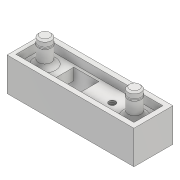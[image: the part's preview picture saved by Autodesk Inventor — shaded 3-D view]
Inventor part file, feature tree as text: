
AUTODESK INVENTOR PART (.ipt)
format: ipt  version: 2018 (Build 220112000, 112)  size: 288,256 bytes
history: native  units: mm
features: sketch x12, projected_geometry x10, extrude x8, hole x2, plane x2, revolve x2, chamfer x1, fillet x1
ambient origin geometry x8: Origin, YZ Plane, XZ Plane, XY Plane, X Axis, Y Axis, Z Axis, Center Point
bodies: Solid1 (feature_tree)
feature tree (38):
  extrude  "Extrusion1"  Depth=7.0mm
  extrude  "Extrusion2"  Depth=4.2mm
  extrude  "Extrusion3"  Depth=6.4mm
  extrude  "Extrusion4"  Depth=0.7mm
  extrude  "Extrusion5"  Depth=5.2mm
  hole  "Hole1"  [1 undecoded]
  extrude  "Extrusion7"  Depth=2.9mm TaperAngle=0.0deg
  hole  "Hole2"  [1 undecoded]
  extrude  "Extrusion8"  Depth=1.0mm
  chamfer  "Chamfer1"  Distance=1.5mm
  plane  "Work Plane1"
  extrude  "Extrusion9"  Depth=0.8mm
  plane  "Work Plane2"
  revolve  "Revolution1"  [1 undecoded]
  revolve  "Revolution2"  [1 undecoded]
  fillet  "Fillet1"  Radius=16.1mm
  sketch  "Sketch1"  dims[d0=22.8mm d1=7.0mm]
  sketch  "Sketch2"  dims[d2=6.0mm d3=0.0mm d4=4.2mm]
  sketch  "Sketch3"  dims[d5=4.5mm d6=6.4mm]
  projected_geometry  "Projected Loop1"
  sketch  "Sketch4"  dims[d7=6.0mm d8=0.0mm d11=0.7mm]
  projected_geometry  "Projected Loop2"
  sketch  "Sketch5"  dims[d12=0.9mm d13=5.2mm]
  sketch  "Sketch6"  dims[d14=21.2mm d15=1.5mm d16=0.0mm]
  projected_geometry  "Projected Loop3"
  sketch  "Sketch7"  dims[d17=14.0mm d18=2.9mm d19=0.0mm]
  projected_geometry  "Projected Loop4"
  sketch  "Sketch8"  dims[d20=12.9mm d21=5.0mm]
  sketch  "Sketch9"  dims[d22=2.4mm d23=0.0mm]
  sketch  "Sketch10"  dims[d24=0.5mm d25=6.0mm d26=3.023mm d27=2.0mm d28=14.3117mm d29=2.4mm d30=0.0mm d36=1.0mm]
  sketch  "Sketch11"  dims[d37=2.2mm]
  projected_geometry  "Projected Loop5"
  projected_geometry  "Projected Loop6"
  projected_geometry  "Projected Loop7"
  projected_geometry  "Projected Loop8"
  projected_geometry  "Projected Loop9"
  projected_geometry  "Projected Loop10"
  sketch  "Sketch12"  dims[d38=2.1mm d39=1.5mm d40=0.0mm d41=3.5mm d42=15.4mm d43=1.181mm d44=3.048mm d45=3.023mm d46=2.0mm d47=14.3117mm d48=4.636mm d49=0.0mm d50=3.5mm d51=16.1mm d52=3.3mm d53=2.3mm d54=4.5mm d55=0.0mm d56=0.3mm d57=2.0mm d58=45.0deg d59=-1.2mm d60=2.4mm d61=2.4mm d62=0.2mm d63=0.0mm d67=-3.5mm d68=3.490659mm d69=45.0deg d70=90.0deg d71=12.217305mm d72=45.0deg d73=90.0deg d74=0.8mm]
note: 4 required parameter values undecoded (feature->parameter linkage not recoverable at this tier; creation-order binding heuristic only, values carry confidence <= 0.55)